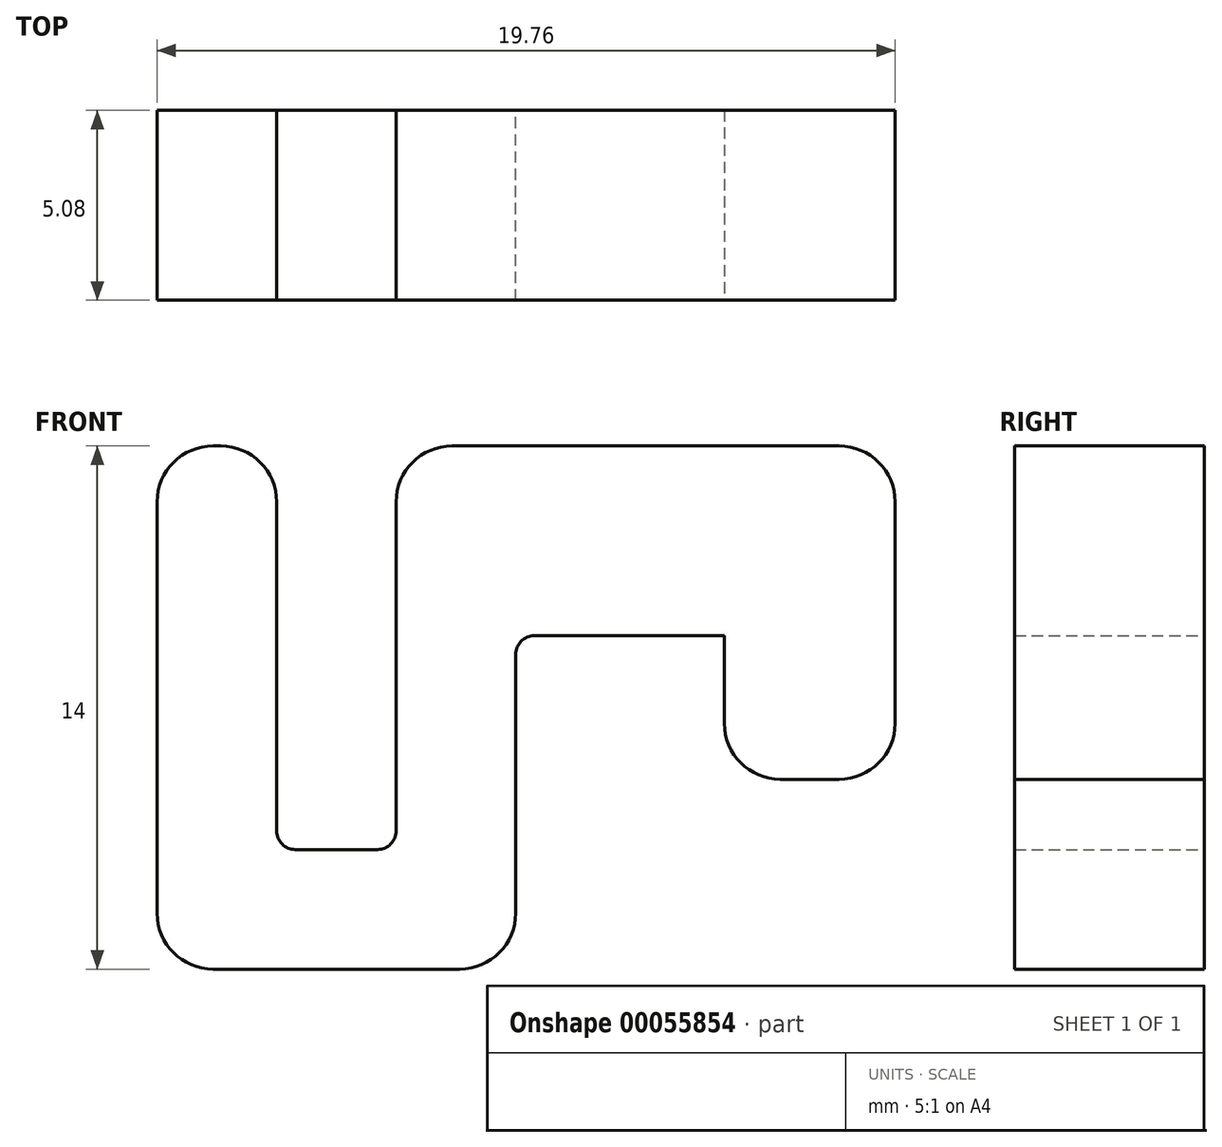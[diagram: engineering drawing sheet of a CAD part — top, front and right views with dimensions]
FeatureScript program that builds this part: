
annotation { "Feature Type Name" : "Feature", "Feature Type Description" : "" }
export const myFeature = defineFeature(function(context is Context, id is Id, definition is map)
    precondition{}
    {
        {
            var Q0;
            Q0=qCreatedBy(makeId("Front.planeOp"),FACE);
            var sketch = newSketch(context, id + "F0", { "sketchPlane" : qUnion([Q0])});
            skLineSegment(sketch, "E0.bottom", {"start": v(1.27, 0) * mm, "end": v(3.2, 0) * mm});
            skLineSegment(sketch, "E0.top", {"start": v(1.27, 14) * mm, "end": v(3.2, 14) * mm});
            skLineSegment(sketch, "E0.left", {"start": v(0, 1.27) * mm, "end": v(0, 12.73) * mm});
            skLineSegment(sketch, "E0.right", {"start": v(3.2, 0) * mm, "end": v(3.2, 14) * mm});
            skLineSegment(sketch, "E1.bottom", {"start": v(3.2, 0) * mm, "end": v(6.4, 0) * mm});
            skLineSegment(sketch, "E1.top", {"start": v(3.2, 3.2) * mm, "end": v(6.4, 3.2) * mm});
            skLineSegment(sketch, "E1.left", {"start": v(3.2, 0) * mm, "end": v(3.2, 3.2) * mm});
            skLineSegment(sketch, "E1.right", {"start": v(6.4, 0) * mm, "end": v(6.4, 3.2) * mm});
            skLineSegment(sketch, "E2.bottom", {"start": v(6.4, 0) * mm, "end": v(8.33, 0) * mm});
            skLineSegment(sketch, "E2.top", {"start": v(6.4, 14) * mm, "end": v(9.6, 14) * mm});
            skLineSegment(sketch, "E2.left", {"start": v(6.4, 0) * mm, "end": v(6.4, 14) * mm});
            skLineSegment(sketch, "E2.right", {"start": v(9.6, 1.27) * mm, "end": v(9.6, 14) * mm});
            skLineSegment(sketch, "E3.bottom", {"start": v(9.6, 14) * mm, "end": v(19.76, 14) * mm});
            skLineSegment(sketch, "E3.top", {"start": v(9.6, 8.92) * mm, "end": v(19.76, 8.92) * mm});
            skLineSegment(sketch, "E3.left", {"start": v(9.6, 14) * mm, "end": v(9.6, 8.92) * mm});
            skLineSegment(sketch, "E3.right", {"start": v(19.76, 14) * mm, "end": v(19.76, 8.92) * mm});
            skPoint(sketch, "E4.visualSharp", {"position": v(0, 14) * mm});
            skArc(sketch, "E4.filletArc", {"start": v(1.27, 14) * mm, "mid": v(0.37, 13.63) * mm, "end": v(0, 12.73) * mm});
            skPoint(sketch, "E5.visualSharp", {"position": v(0, 0) * mm});
            skArc(sketch, "E5.filletArc", {"start": v(0, 1.27) * mm, "mid": v(0.37, 0.37) * mm, "end": v(1.27, 0) * mm});
            skPoint(sketch, "E6.visualSharp", {"position": v(9.6, 0) * mm});
            skArc(sketch, "E6.filletArc", {"start": v(8.33, 0) * mm, "mid": v(9.23, 0.37) * mm, "end": v(9.6, 1.27) * mm});
            skLineSegment(sketch, "E7", {"start": v(0, 10.8) * mm, "end": v(3.2, 10.8) * mm});
            skLineSegment(sketch, "E8", {"start": v(0, 0) * mm, "end": v(0, 1.27) * mm});
            skLineSegment(sketch, "E9", {"start": v(0, 0) * mm, "end": v(1.27, 0) * mm});
            skLineSegment(sketch, "E10", {"start": v(9.6, 0) * mm, "end": v(8.33, 0) * mm});
            skLineSegment(sketch, "E11", {"start": v(9.6, 0) * mm, "end": v(9.6, 1.27) * mm});
            skLineSegment(sketch, "E12", {"start": v(0, 12.73) * mm, "end": v(0, 14) * mm});
            skLineSegment(sketch, "E13", {"start": v(1.27, 14) * mm, "end": v(0, 14) * mm});
            skSolve(sketch);
        }
        {
            var Q0;
            Q0=makeQuery(id+"F0.imprint","IMPRINT",FACE,{"disambiguationData":[TD([[makeQuery(id+"F0.imprint","IMPRINT",EDGE,{"derivedFrom":sQuery(id+"F0.wireOp",EDGE,"E3.bottom")}),-1.0]])]});
            var Q1;
            Q1=makeQuery(id+"F0.imprint","IMPRINT",FACE,{"disambiguationData":[TD([[makeQuery(id+"F0.imprint","IMPRINT",EDGE,{"derivedFrom":sQuery(id+"F0.wireOp",EDGE,"E0.bottom")}),1.0]])]});
            var Q2;
            {var subQ0=sQuery(id+"F0.wireOp",EDGE,"E1.bottom");Q2=makeQuery(id+"F0.imprint","IMPRINT",FACE,{"disambiguationData":[TD([[makeQuery(id+"F0.imprint","IMPRINT",EDGE,{"derivedFrom":subQ0}),1.0]])]});}
            var Q3;
            {var subQ3=sQuery(id+"F0.wireOp",EDGE,"E2.bottom");Q3=makeQuery(id+"F0.imprint","IMPRINT",FACE,{"disambiguationData":[TD([[makeQuery(id+"F0.imprint","IMPRINT",EDGE,{"derivedFrom":subQ3}),1.0]])]});}
            var Q4;
            Q4=makeQuery(id+"F0.imprint","IMPRINT",FACE,{"disambiguationData":[TD([[makeQuery(id+"F0.imprint","IMPRINT",EDGE,{"derivedFrom":sQuery(id+"F0.wireOp",EDGE,"E5.filletArc")}),-1.0]])]});
            var Q5;
            Q5=makeQuery(id+"F0.imprint","IMPRINT",FACE,{"disambiguationData":[TD([[makeQuery(id+"F0.imprint","IMPRINT",EDGE,{"derivedFrom":sQuery(id+"F0.wireOp",EDGE,"E6.filletArc")}),-1.0]])]});
            var Q6;
            {var subQ1=sQuery(id+"F0.wireOp",EDGE,"E0.top");Q6=makeQuery(id+"F0.imprint","IMPRINT",FACE,{"disambiguationData":[TD([[makeQuery(id+"F0.imprint","IMPRINT",EDGE,{"derivedFrom":subQ1}),-1.0]])]});}
            var Q7;
            Q7=makeQuery(id+"F0.imprint","IMPRINT",FACE,{"disambiguationData":[TD([[makeQuery(id+"F0.imprint","IMPRINT",EDGE,{"derivedFrom":sQuery(id+"F0.wireOp",EDGE,"E4.filletArc")}),-1.0]])]});
            extrude(context, id + "F1", {"entities" : qUnion([Q0, Q1, Q2, Q3, Q4, Q5, Q6, Q7]), "depth" : 5.08 * mm});
        }
        {
            var Q0;
            Q0=makeQuery(id+"F1.opExtrude","SWEPT_FACE",FACE,{"disambiguationData":[OSD([sQuery(id+"F0.wireOp",EDGE,"E3.top")])]});
            var sketch = newSketch(context, id + "F2", { "sketchPlane" : qUnion([Q0])});
            skLineSegment(sketch, "E14.bottom", {"start": v(19.76, 5.08) * mm, "end": v(15.19, 5.08) * mm});
            skLineSegment(sketch, "E14.top", {"start": v(19.76, 0) * mm, "end": v(15.19, 0) * mm});
            skLineSegment(sketch, "E14.left", {"start": v(19.76, 5.08) * mm, "end": v(19.76, 0) * mm});
            skLineSegment(sketch, "E14.right", {"start": v(15.19, 0) * mm, "end": v(15.19, 5.08) * mm});
            skSolve(sketch);
        }
        {
            var Q0;
            Q0=makeQuery(id+"F2.imprint","IMPRINT",FACE,{"disambiguationData":[TD([[makeQuery(id+"F2.imprint","IMPRINT",EDGE,{"derivedFrom":sQuery(id+"F2.wireOp",EDGE,"E14.bottom")}),-1.0]])]});
            extrude(context, id + "F3", {"entities" : qUnion([Q0]), "operationType" : NewBodyOperationType.ADD, "depth" : (14 - 2 * 5.08) * mm});
        }
        {
            var Q0;
            Q0=makeQuery(id+"F1.opExtrude","SWEPT_EDGE",EDGE,{"disambiguationData":[OSD([sQuery(id+"F0.wireOp",EDGE,"E8"),sQuery(id+"F0.wireOp",EDGE,"E9")])]});
            var Q1;
            Q1=makeQuery(id+"F1.opExtrude","SWEPT_EDGE",EDGE,{"disambiguationData":[OSD([sQuery(id+"F0.wireOp",EDGE,"E10"),sQuery(id+"F0.wireOp",EDGE,"E11")])]});
            var Q2;
            Q2=makeQuery(id+"F1.opExtrude","SWEPT_EDGE",EDGE,{"disambiguationData":[OSD([sQuery(id+"F0.wireOp",EDGE,"E12"),sQuery(id+"F0.wireOp",EDGE,"E13")])]});
            var Q3;
            Q3=makeQuery(id+"F1.opExtrude","SWEPT_EDGE",EDGE,{"disambiguationData":[OSD([sQuery(id+"F0.wireOp",EDGE,"E0.top"),sQuery(id+"F0.wireOp",EDGE,"E0.right")])]});
            var Q4;
            Q4=makeQuery(id+"F1.opExtrude","SWEPT_EDGE",EDGE,{"disambiguationData":[OSD([sQuery(id+"F0.wireOp",EDGE,"E2.top"),sQuery(id+"F0.wireOp",EDGE,"E2.left")])]});
            var Q5;
            Q5=makeQuery(id+"F1.opExtrude","SWEPT_EDGE",EDGE,{"disambiguationData":[OSD([sQuery(id+"F0.wireOp",EDGE,"E3.bottom"),sQuery(id+"F0.wireOp",EDGE,"E3.right")])]});
            var Q6;
            Q6=makeQuery(id+"F3.opExtrude","CAP_EDGE",EDGE,{"disambiguationData":[OSD([sQuery(id+"F2.wireOp",EDGE,"E14.left")])],"isStart":false});
            var Q7;
            Q7=makeQuery(id+"F3.opExtrude","CAP_EDGE",EDGE,{"disambiguationData":[OSD([sQuery(id+"F2.wireOp",EDGE,"E14.right")])],"isStart":false});
            fillet(context, id + "F4", {"entities" : qUnion([Q0, Q1, Q2, Q3, Q4, Q5, Q6, Q7]), "radius" : 1.5 * mm, "tangentPropagation" : true, "allowEdgeOverflow" : false});
        }
        {
            var Q0;
            Q0=makeQuery(id+"F1.opExtrude","SWEPT_EDGE",EDGE,{"disambiguationData":[OSD([sQuery(id+"F0.wireOp",EDGE,"E1.top"),sQuery(id+"F0.wireOp",EDGE,"E2.left")])]});
            var Q1;
            Q1=makeQuery(id+"F1.opExtrude","SWEPT_EDGE",EDGE,{"disambiguationData":[OSD([sQuery(id+"F0.wireOp",EDGE,"E0.right"),sQuery(id+"F0.wireOp",EDGE,"E1.top"),sQuery(id+"F0.wireOp",EDGE,"E1.left")])]});
            var Q2;
            Q2=makeQuery(id+"F3.opExtrude","CAP_EDGE",EDGE,{"disambiguationData":[OSD([sQuery(id+"F2.wireOp",EDGE,"E14.right")])],"isStart":true});
            var Q3;
            Q3=makeQuery(id+"F1.opExtrude","SWEPT_EDGE",EDGE,{"disambiguationData":[OSD([sQuery(id+"F0.wireOp",EDGE,"E2.right"),sQuery(id+"F0.wireOp",EDGE,"E3.top"),sQuery(id+"F0.wireOp",EDGE,"E3.left")])]});
            fillet(context, id + "F5", {"entities" : qUnion([Q0, Q1, Q2, Q3]), "radius" : .5 * mm, "tangentPropagation" : true, "allowEdgeOverflow" : false});
        }
    });
